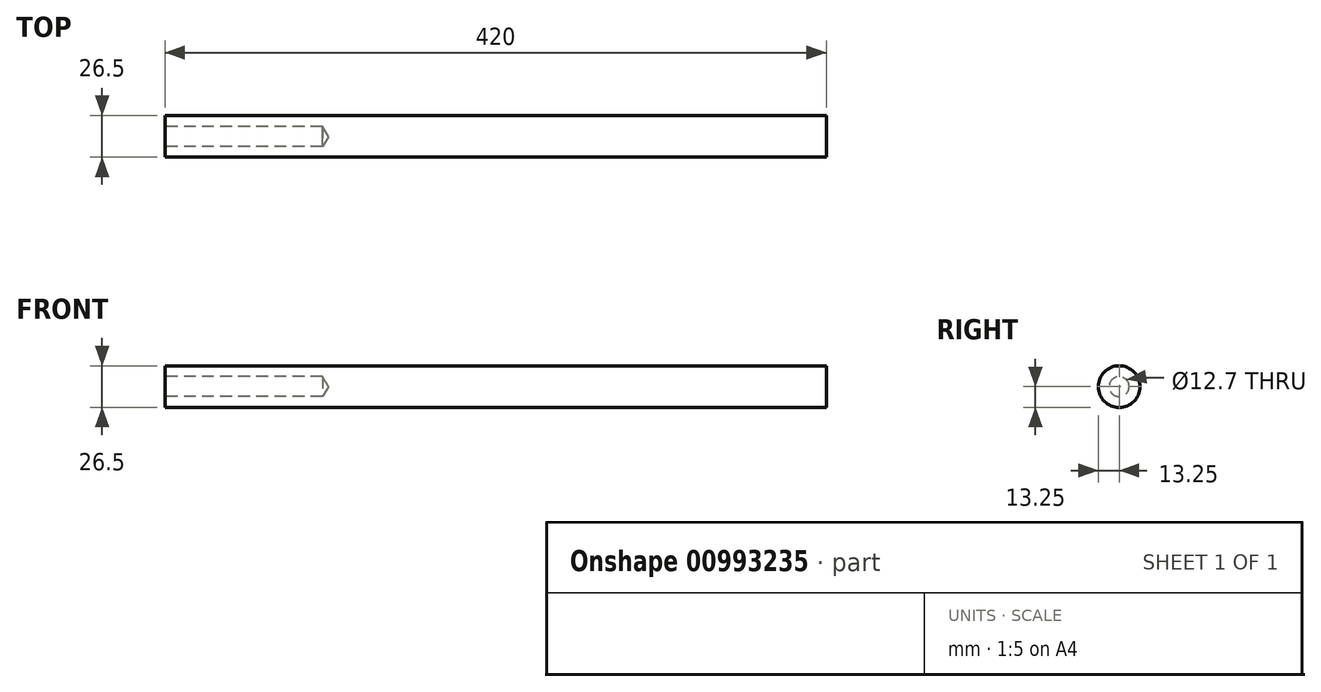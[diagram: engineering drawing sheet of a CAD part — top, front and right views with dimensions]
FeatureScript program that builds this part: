
annotation { "Feature Type Name" : "Feature", "Feature Type Description" : "" }
export const myFeature = defineFeature(function(context is Context, id is Id, definition is map)
    precondition{}
    {
        {
            var Q0;
            Q0=qCreatedBy(makeId("Top.planeOp"),FACE);
            var sketch = newSketch(context, id + "F0", { "sketchPlane" : qUnion([Q0])});
            skLineSegment(sketch, "E0", {"start": v(-210, 0) * mm, "end": v(210, 0) * mm});
            skSolve(sketch);
        }
        {
            var Q0;
            Q0=qCreatedBy(makeId("Right.planeOp"),FACE);
            var sketch = newSketch(context, id + "F1", { "sketchPlane" : qUnion([Q0])});
            skCircle(sketch, "E1", {"center": v(0, 0) * mm, "radius": 13.25 * mm});
            skSolve(sketch);
        }
        {
            var Q0;
            Q0=makeQuery(id+"F1.imprint","IMPRINT",FACE,{"disambiguationData":[TD([[makeQuery(id+"F1.imprint","IMPRINT",EDGE,{"derivedFrom":sQuery(id+"F1.wireOp",EDGE,"E1")}),1.0]])]});
            var Q1;
            Q1=sQuery(id+"F0.wireOp",EDGE,"E0");
            sweep(context, id + "F2", {"profiles" : qUnion([Q0]), "path" : qUnion([Q1])});
        }
        {
            var Q0;
            Q0=makeQuery(id+"F2.opSweep","CAP_FACE",FACE,{"disambiguationData":[OSD([sQuery(id+"F0.wireOp",VERTEX,"E0.start"),sQuery(id+"F1.wireOp",EDGE,"E1")])],"isStart":true});
            var sketch = newSketch(context, id + "F3", { "sketchPlane" : qUnion([Q0])});
            skPoint(sketch, "E2", {"position": v(0, 0) * mm});
            skSolve(sketch);
        }
        {
            var Q0;
            Q0=sQuery(id+"F3.wireOp",VERTEX,"E2");
            var Q1;
            Q1=makeQuery(id+"F2.opSweep","SWEPT_BODY",BODY,{"disambiguationData":[OSD([sQuery(id+"F0.wireOp",EDGE,"E0"),sQuery(id+"F1.wireOp",EDGE,"E1")])]});
            hole(context, id + "F4", {"style" : HoleStyle.SIMPLE, "endStyle" : HoleEndStyle.BLIND, "holeDiameter" : 12.7 * mm, "majorDiameter" : 5 * mm, "holeDepth" : 100 * mm, "isTappedThrough" : true, "tappedDepth" : 12 * mm, "tapClearance" : 3, "locations" : qUnion([Q0]), "scope" : qUnion([Q1])});
        }
    });
